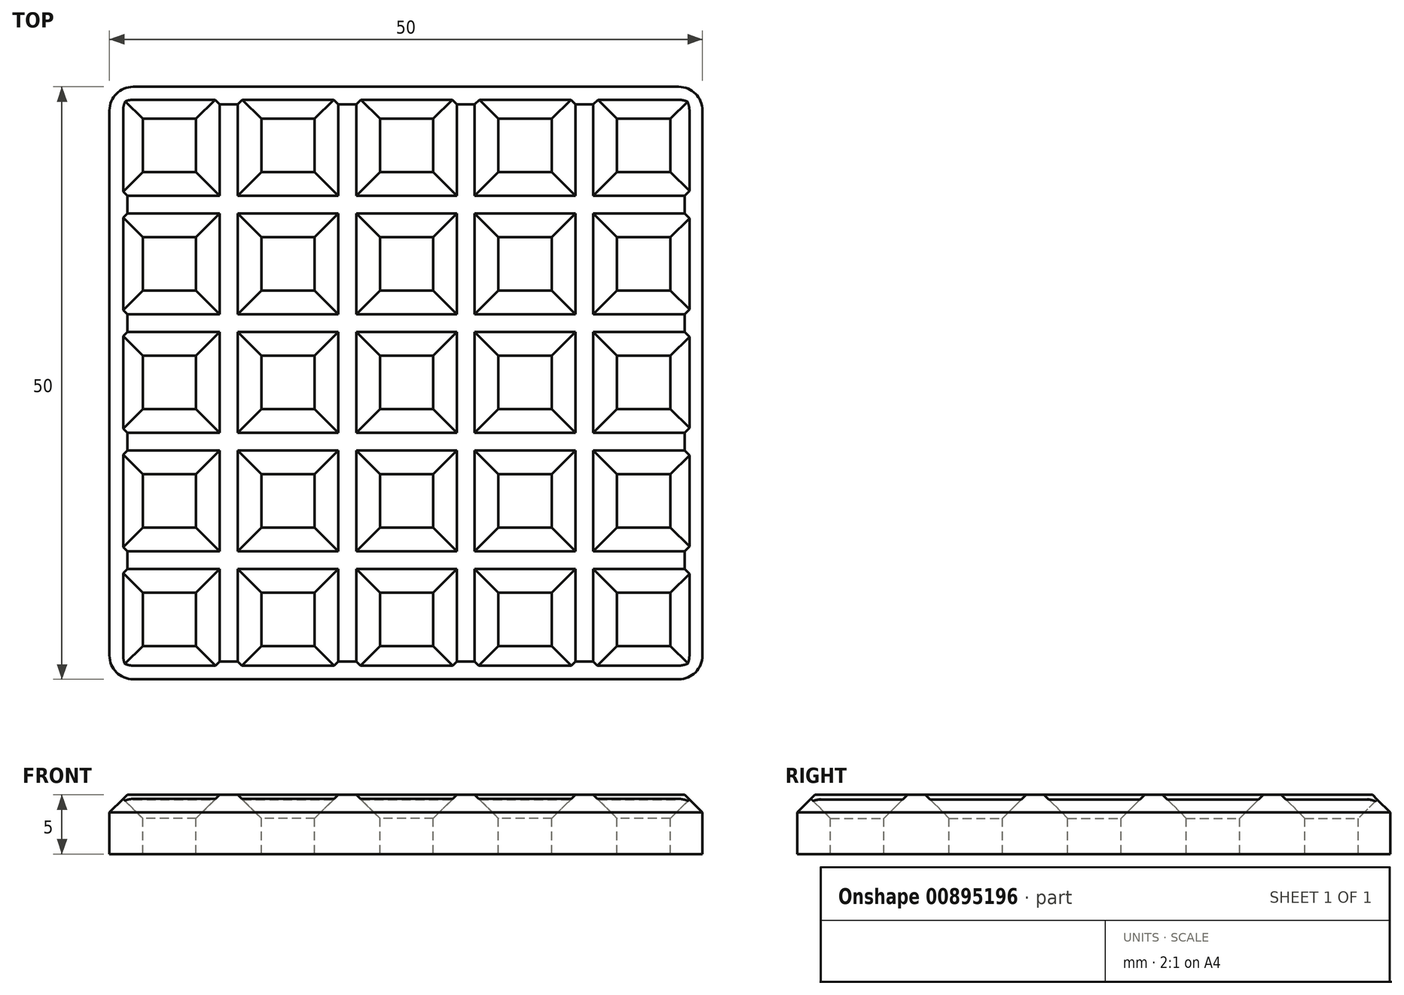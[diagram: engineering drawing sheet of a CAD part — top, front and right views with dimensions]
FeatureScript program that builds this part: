
annotation { "Feature Type Name" : "Feature", "Feature Type Description" : "" }
export const myFeature = defineFeature(function(context is Context, id is Id, definition is map)
    precondition{}
    {
        {
            var Q0;
            Q0=qCreatedBy(makeId("Top.planeOp"),FACE);
            var sketch = newSketch(context, id + "F0", { "sketchPlane" : qUnion([Q0])});
            skLineSegment(sketch, "E0.bottom", {"start": v(25, 25) * mm, "end": v(-25, 25) * mm});
            skLineSegment(sketch, "E0.top", {"start": v(25, -25) * mm, "end": v(-25, -25) * mm});
            skLineSegment(sketch, "E0.left", {"start": v(25, 25) * mm, "end": v(25, -25) * mm});
            skLineSegment(sketch, "E0.right", {"start": v(-25, 25) * mm, "end": v(-25, -25) * mm});
            skPoint(sketch, "E0.middle", {"position": v(0, 0) * mm});
            skLineSegment(sketch, "E1.bottom", {"start": v(-17.7, -17.7) * mm, "end": v(-22.2, -17.7) * mm});
            skLineSegment(sketch, "E1.top", {"start": v(-17.7, -22.2) * mm, "end": v(-22.2, -22.2) * mm});
            skLineSegment(sketch, "E1.left", {"start": v(-17.7, -17.7) * mm, "end": v(-17.7, -22.2) * mm});
            skLineSegment(sketch, "E1.right", {"start": v(-22.2, -17.7) * mm, "end": v(-22.2, -22.2) * mm});
            skPoint(sketch, "E1.middle", {"position": v(-19.95, -19.95) * mm});
            skLineSegment(sketch, "E2.0.1.0", {"start": v(-17.7, -7.7) * mm, "end": v(-17.7, -12.2) * mm});
            skLineSegment(sketch, "E2.0.1.1", {"start": v(-17.7, -7.7) * mm, "end": v(-22.2, -7.7) * mm});
            skLineSegment(sketch, "E2.0.1.2", {"start": v(-22.2, -7.7) * mm, "end": v(-22.2, -12.2) * mm});
            skLineSegment(sketch, "E2.0.1.3", {"start": v(-17.7, -12.2) * mm, "end": v(-22.2, -12.2) * mm});
            skLineSegment(sketch, "E2.0.2.0", {"start": v(-17.7, 2.3) * mm, "end": v(-17.7, -2.2) * mm});
            skLineSegment(sketch, "E2.0.2.1", {"start": v(-17.7, 2.3) * mm, "end": v(-22.2, 2.3) * mm});
            skLineSegment(sketch, "E2.0.2.2", {"start": v(-22.2, 2.3) * mm, "end": v(-22.2, -2.2) * mm});
            skLineSegment(sketch, "E2.0.2.3", {"start": v(-17.7, -2.2) * mm, "end": v(-22.2, -2.2) * mm});
            skLineSegment(sketch, "E2.0.3.0", {"start": v(-17.7, 12.3) * mm, "end": v(-17.7, 7.8) * mm});
            skLineSegment(sketch, "E2.0.3.1", {"start": v(-17.7, 12.3) * mm, "end": v(-22.2, 12.3) * mm});
            skLineSegment(sketch, "E2.0.3.2", {"start": v(-22.2, 12.3) * mm, "end": v(-22.2, 7.8) * mm});
            skLineSegment(sketch, "E2.0.3.3", {"start": v(-17.7, 7.8) * mm, "end": v(-22.2, 7.8) * mm});
            skLineSegment(sketch, "E2.0.4.0", {"start": v(-17.7, 22.3) * mm, "end": v(-17.7, 17.8) * mm});
            skLineSegment(sketch, "E2.0.4.1", {"start": v(-17.7, 22.3) * mm, "end": v(-22.2, 22.3) * mm});
            skLineSegment(sketch, "E2.0.4.2", {"start": v(-22.2, 22.3) * mm, "end": v(-22.2, 17.8) * mm});
            skLineSegment(sketch, "E2.0.4.3", {"start": v(-17.7, 17.8) * mm, "end": v(-22.2, 17.8) * mm});
            skLineSegment(sketch, "E2.1.0.0", {"start": v(-7.7, -17.7) * mm, "end": v(-7.7, -22.2) * mm});
            skLineSegment(sketch, "E2.1.0.1", {"start": v(-7.7, -17.7) * mm, "end": v(-12.2, -17.7) * mm});
            skLineSegment(sketch, "E2.1.0.2", {"start": v(-12.2, -17.7) * mm, "end": v(-12.2, -22.2) * mm});
            skLineSegment(sketch, "E2.1.0.3", {"start": v(-7.7, -22.2) * mm, "end": v(-12.2, -22.2) * mm});
            skLineSegment(sketch, "E2.1.1.0", {"start": v(-7.7, -7.7) * mm, "end": v(-7.7, -12.2) * mm});
            skLineSegment(sketch, "E2.1.1.1", {"start": v(-7.7, -7.7) * mm, "end": v(-12.2, -7.7) * mm});
            skLineSegment(sketch, "E2.1.1.2", {"start": v(-12.2, -7.7) * mm, "end": v(-12.2, -12.2) * mm});
            skLineSegment(sketch, "E2.1.1.3", {"start": v(-7.7, -12.2) * mm, "end": v(-12.2, -12.2) * mm});
            skLineSegment(sketch, "E2.1.2.0", {"start": v(-7.7, 2.3) * mm, "end": v(-7.7, -2.2) * mm});
            skLineSegment(sketch, "E2.1.2.1", {"start": v(-7.7, 2.3) * mm, "end": v(-12.2, 2.3) * mm});
            skLineSegment(sketch, "E2.1.2.2", {"start": v(-12.2, 2.3) * mm, "end": v(-12.2, -2.2) * mm});
            skLineSegment(sketch, "E2.1.2.3", {"start": v(-7.7, -2.2) * mm, "end": v(-12.2, -2.2) * mm});
            skLineSegment(sketch, "E2.1.3.0", {"start": v(-7.7, 12.3) * mm, "end": v(-7.7, 7.8) * mm});
            skLineSegment(sketch, "E2.1.3.1", {"start": v(-7.7, 12.3) * mm, "end": v(-12.2, 12.3) * mm});
            skLineSegment(sketch, "E2.1.3.2", {"start": v(-12.2, 12.3) * mm, "end": v(-12.2, 7.8) * mm});
            skLineSegment(sketch, "E2.1.3.3", {"start": v(-7.7, 7.8) * mm, "end": v(-12.2, 7.8) * mm});
            skLineSegment(sketch, "E2.1.4.0", {"start": v(-7.7, 22.3) * mm, "end": v(-7.7, 17.8) * mm});
            skLineSegment(sketch, "E2.1.4.1", {"start": v(-7.7, 22.3) * mm, "end": v(-12.2, 22.3) * mm});
            skLineSegment(sketch, "E2.1.4.2", {"start": v(-12.2, 22.3) * mm, "end": v(-12.2, 17.8) * mm});
            skLineSegment(sketch, "E2.1.4.3", {"start": v(-7.7, 17.8) * mm, "end": v(-12.2, 17.8) * mm});
            skLineSegment(sketch, "E2.2.0.0", {"start": v(2.3, -17.7) * mm, "end": v(2.3, -22.2) * mm});
            skLineSegment(sketch, "E2.2.0.1", {"start": v(2.3, -17.7) * mm, "end": v(-2.2, -17.7) * mm});
            skLineSegment(sketch, "E2.2.0.2", {"start": v(-2.2, -17.7) * mm, "end": v(-2.2, -22.2) * mm});
            skLineSegment(sketch, "E2.2.0.3", {"start": v(2.3, -22.2) * mm, "end": v(-2.2, -22.2) * mm});
            skLineSegment(sketch, "E2.2.1.0", {"start": v(2.3, -7.7) * mm, "end": v(2.3, -12.2) * mm});
            skLineSegment(sketch, "E2.2.1.1", {"start": v(2.3, -7.7) * mm, "end": v(-2.2, -7.7) * mm});
            skLineSegment(sketch, "E2.2.1.2", {"start": v(-2.2, -7.7) * mm, "end": v(-2.2, -12.2) * mm});
            skLineSegment(sketch, "E2.2.1.3", {"start": v(2.3, -12.2) * mm, "end": v(-2.2, -12.2) * mm});
            skLineSegment(sketch, "E2.2.2.0", {"start": v(2.3, 2.3) * mm, "end": v(2.3, -2.2) * mm});
            skLineSegment(sketch, "E2.2.2.1", {"start": v(2.3, 2.3) * mm, "end": v(-2.2, 2.3) * mm});
            skLineSegment(sketch, "E2.2.2.2", {"start": v(-2.2, 2.3) * mm, "end": v(-2.2, -2.2) * mm});
            skLineSegment(sketch, "E2.2.2.3", {"start": v(2.3, -2.2) * mm, "end": v(-2.2, -2.2) * mm});
            skLineSegment(sketch, "E2.2.3.0", {"start": v(2.3, 12.3) * mm, "end": v(2.3, 7.8) * mm});
            skLineSegment(sketch, "E2.2.3.1", {"start": v(2.3, 12.3) * mm, "end": v(-2.2, 12.3) * mm});
            skLineSegment(sketch, "E2.2.3.2", {"start": v(-2.2, 12.3) * mm, "end": v(-2.2, 7.8) * mm});
            skLineSegment(sketch, "E2.2.3.3", {"start": v(2.3, 7.8) * mm, "end": v(-2.2, 7.8) * mm});
            skLineSegment(sketch, "E2.2.4.0", {"start": v(2.3, 22.3) * mm, "end": v(2.3, 17.8) * mm});
            skLineSegment(sketch, "E2.2.4.1", {"start": v(2.3, 22.3) * mm, "end": v(-2.2, 22.3) * mm});
            skLineSegment(sketch, "E2.2.4.2", {"start": v(-2.2, 22.3) * mm, "end": v(-2.2, 17.8) * mm});
            skLineSegment(sketch, "E2.2.4.3", {"start": v(2.3, 17.8) * mm, "end": v(-2.2, 17.8) * mm});
            skLineSegment(sketch, "E2.3.0.0", {"start": v(12.3, -17.7) * mm, "end": v(12.3, -22.2) * mm});
            skLineSegment(sketch, "E2.3.0.1", {"start": v(12.3, -17.7) * mm, "end": v(7.8, -17.7) * mm});
            skLineSegment(sketch, "E2.3.0.2", {"start": v(7.8, -17.7) * mm, "end": v(7.8, -22.2) * mm});
            skLineSegment(sketch, "E2.3.0.3", {"start": v(12.3, -22.2) * mm, "end": v(7.8, -22.2) * mm});
            skLineSegment(sketch, "E2.3.1.0", {"start": v(12.3, -7.7) * mm, "end": v(12.3, -12.2) * mm});
            skLineSegment(sketch, "E2.3.1.1", {"start": v(12.3, -7.7) * mm, "end": v(7.8, -7.7) * mm});
            skLineSegment(sketch, "E2.3.1.2", {"start": v(7.8, -7.7) * mm, "end": v(7.8, -12.2) * mm});
            skLineSegment(sketch, "E2.3.1.3", {"start": v(12.3, -12.2) * mm, "end": v(7.8, -12.2) * mm});
            skLineSegment(sketch, "E2.3.2.0", {"start": v(12.3, 2.3) * mm, "end": v(12.3, -2.2) * mm});
            skLineSegment(sketch, "E2.3.2.1", {"start": v(12.3, 2.3) * mm, "end": v(7.8, 2.3) * mm});
            skLineSegment(sketch, "E2.3.2.2", {"start": v(7.8, 2.3) * mm, "end": v(7.8, -2.2) * mm});
            skLineSegment(sketch, "E2.3.2.3", {"start": v(12.3, -2.2) * mm, "end": v(7.8, -2.2) * mm});
            skLineSegment(sketch, "E2.3.3.0", {"start": v(12.3, 12.3) * mm, "end": v(12.3, 7.8) * mm});
            skLineSegment(sketch, "E2.3.3.1", {"start": v(12.3, 12.3) * mm, "end": v(7.8, 12.3) * mm});
            skLineSegment(sketch, "E2.3.3.2", {"start": v(7.8, 12.3) * mm, "end": v(7.8, 7.8) * mm});
            skLineSegment(sketch, "E2.3.3.3", {"start": v(12.3, 7.8) * mm, "end": v(7.8, 7.8) * mm});
            skLineSegment(sketch, "E2.3.4.0", {"start": v(12.3, 22.3) * mm, "end": v(12.3, 17.8) * mm});
            skLineSegment(sketch, "E2.3.4.1", {"start": v(12.3, 22.3) * mm, "end": v(7.8, 22.3) * mm});
            skLineSegment(sketch, "E2.3.4.2", {"start": v(7.8, 22.3) * mm, "end": v(7.8, 17.8) * mm});
            skLineSegment(sketch, "E2.3.4.3", {"start": v(12.3, 17.8) * mm, "end": v(7.8, 17.8) * mm});
            skLineSegment(sketch, "E2.4.0.0", {"start": v(22.3, -17.7) * mm, "end": v(22.3, -22.2) * mm});
            skLineSegment(sketch, "E2.4.0.1", {"start": v(22.3, -17.7) * mm, "end": v(17.8, -17.7) * mm});
            skLineSegment(sketch, "E2.4.0.2", {"start": v(17.8, -17.7) * mm, "end": v(17.8, -22.2) * mm});
            skLineSegment(sketch, "E2.4.0.3", {"start": v(22.3, -22.2) * mm, "end": v(17.8, -22.2) * mm});
            skLineSegment(sketch, "E2.4.1.0", {"start": v(22.3, -7.7) * mm, "end": v(22.3, -12.2) * mm});
            skLineSegment(sketch, "E2.4.1.1", {"start": v(22.3, -7.7) * mm, "end": v(17.8, -7.7) * mm});
            skLineSegment(sketch, "E2.4.1.2", {"start": v(17.8, -7.7) * mm, "end": v(17.8, -12.2) * mm});
            skLineSegment(sketch, "E2.4.1.3", {"start": v(22.3, -12.2) * mm, "end": v(17.8, -12.2) * mm});
            skLineSegment(sketch, "E2.4.2.0", {"start": v(22.3, 2.3) * mm, "end": v(22.3, -2.2) * mm});
            skLineSegment(sketch, "E2.4.2.1", {"start": v(22.3, 2.3) * mm, "end": v(17.8, 2.3) * mm});
            skLineSegment(sketch, "E2.4.2.2", {"start": v(17.8, 2.3) * mm, "end": v(17.8, -2.2) * mm});
            skLineSegment(sketch, "E2.4.2.3", {"start": v(22.3, -2.2) * mm, "end": v(17.8, -2.2) * mm});
            skLineSegment(sketch, "E2.4.3.0", {"start": v(22.3, 12.3) * mm, "end": v(22.3, 7.8) * mm});
            skLineSegment(sketch, "E2.4.3.1", {"start": v(22.3, 12.3) * mm, "end": v(17.8, 12.3) * mm});
            skLineSegment(sketch, "E2.4.3.2", {"start": v(17.8, 12.3) * mm, "end": v(17.8, 7.8) * mm});
            skLineSegment(sketch, "E2.4.3.3", {"start": v(22.3, 7.8) * mm, "end": v(17.8, 7.8) * mm});
            skLineSegment(sketch, "E2.4.4.0", {"start": v(22.3, 22.3) * mm, "end": v(22.3, 17.8) * mm});
            skLineSegment(sketch, "E2.4.4.1", {"start": v(22.3, 22.3) * mm, "end": v(17.8, 22.3) * mm});
            skLineSegment(sketch, "E2.4.4.2", {"start": v(17.8, 22.3) * mm, "end": v(17.8, 17.8) * mm});
            skLineSegment(sketch, "E2.4.4.3", {"start": v(22.3, 17.8) * mm, "end": v(17.8, 17.8) * mm});
            skLineSegment(sketch, "E2.direction1", {"start": v(-17.7, -22.2) * mm, "end": v(-7.7, -22.2) * mm, "construction": true});
            skLineSegment(sketch, "E2.direction2", {"start": v(-17.7, -22.2) * mm, "end": v(-17.7, -12.2) * mm, "construction": true});
            skSolve(sketch);
        }
        {
            var Q0;
            Q0=makeQuery(id+"F0.imprint","IMPRINT",FACE,{"disambiguationData":[TD([[makeQuery(id+"F0.imprint","IMPRINT",EDGE,{"derivedFrom":sQuery(id+"F0.wireOp",EDGE,"E0.bottom")}),1.0]])]});
            extrude(context, id + "F1", {"entities" : qUnion([Q0]), "oppositeDirection" : true, "depth" : 5 * mm, "offsetDistance" : 25 * mm});
        }
        {
            var Q0;
            Q0=makeQuery(id+"F1.opExtrude","CAP_EDGE",EDGE,{"disambiguationData":[OSD([sQuery(id+"F0.wireOp",EDGE,"E2.0.1.2")])],"isStart":true});
            var Q1;
            Q1=makeQuery(id+"F1.opExtrude","CAP_EDGE",EDGE,{"disambiguationData":[OSD([sQuery(id+"F0.wireOp",EDGE,"E1.right")])],"isStart":true});
            var Q2;
            Q2=makeQuery(id+"F1.opExtrude","CAP_EDGE",EDGE,{"disambiguationData":[OSD([sQuery(id+"F0.wireOp",EDGE,"E1.top")])],"isStart":true});
            var Q3;
            Q3=makeQuery(id+"F1.opExtrude","CAP_EDGE",EDGE,{"disambiguationData":[OSD([sQuery(id+"F0.wireOp",EDGE,"E1.left")])],"isStart":true});
            var Q4;
            Q4=makeQuery(id+"F1.opExtrude","CAP_EDGE",EDGE,{"disambiguationData":[OSD([sQuery(id+"F0.wireOp",EDGE,"E1.bottom")])],"isStart":true});
            var Q5;
            Q5=makeQuery(id+"F1.opExtrude","CAP_EDGE",EDGE,{"disambiguationData":[OSD([sQuery(id+"F0.wireOp",EDGE,"E2.0.1.0")])],"isStart":true});
            var Q6;
            Q6=makeQuery(id+"F1.opExtrude","CAP_EDGE",EDGE,{"disambiguationData":[OSD([sQuery(id+"F0.wireOp",EDGE,"E2.0.1.1")])],"isStart":true});
            var Q7;
            Q7=makeQuery(id+"F1.opExtrude","CAP_EDGE",EDGE,{"disambiguationData":[OSD([sQuery(id+"F0.wireOp",EDGE,"E2.0.2.1")])],"isStart":true});
            var Q8;
            Q8=makeQuery(id+"F1.opExtrude","CAP_EDGE",EDGE,{"disambiguationData":[OSD([sQuery(id+"F0.wireOp",EDGE,"E2.0.2.2")])],"isStart":true});
            var Q9;
            Q9=makeQuery(id+"F1.opExtrude","CAP_EDGE",EDGE,{"disambiguationData":[OSD([sQuery(id+"F0.wireOp",EDGE,"E2.1.2.3")])],"isStart":true});
            var Q10;
            Q10=makeQuery(id+"F1.opExtrude","CAP_EDGE",EDGE,{"disambiguationData":[OSD([sQuery(id+"F0.wireOp",EDGE,"E2.1.2.1")])],"isStart":true});
            var Q11;
            Q11=makeQuery(id+"F1.opExtrude","CAP_EDGE",EDGE,{"disambiguationData":[OSD([sQuery(id+"F0.wireOp",EDGE,"E2.1.2.2")])],"isStart":true});
            var Q12;
            Q12=makeQuery(id+"F1.opExtrude","CAP_EDGE",EDGE,{"disambiguationData":[OSD([sQuery(id+"F0.wireOp",EDGE,"E2.1.2.0")])],"isStart":true});
            var Q13;
            Q13=makeQuery(id+"F1.opExtrude","CAP_EDGE",EDGE,{"disambiguationData":[OSD([sQuery(id+"F0.wireOp",EDGE,"E2.1.1.1")])],"isStart":true});
            var Q14;
            Q14=makeQuery(id+"F1.opExtrude","CAP_EDGE",EDGE,{"disambiguationData":[OSD([sQuery(id+"F0.wireOp",EDGE,"E2.1.1.3")])],"isStart":true});
            var Q15;
            Q15=makeQuery(id+"F1.opExtrude","CAP_EDGE",EDGE,{"disambiguationData":[OSD([sQuery(id+"F0.wireOp",EDGE,"E2.1.1.2")])],"isStart":true});
            var Q16;
            Q16=makeQuery(id+"F1.opExtrude","CAP_EDGE",EDGE,{"disambiguationData":[OSD([sQuery(id+"F0.wireOp",EDGE,"E2.1.1.0")])],"isStart":true});
            var Q17;
            Q17=makeQuery(id+"F1.opExtrude","CAP_EDGE",EDGE,{"disambiguationData":[OSD([sQuery(id+"F0.wireOp",EDGE,"E2.1.0.1")])],"isStart":true});
            var Q18;
            Q18=makeQuery(id+"F1.opExtrude","CAP_EDGE",EDGE,{"disambiguationData":[OSD([sQuery(id+"F0.wireOp",EDGE,"E2.1.0.2")])],"isStart":true});
            var Q19;
            Q19=makeQuery(id+"F1.opExtrude","CAP_EDGE",EDGE,{"disambiguationData":[OSD([sQuery(id+"F0.wireOp",EDGE,"E2.1.0.3")])],"isStart":true});
            var Q20;
            Q20=makeQuery(id+"F1.opExtrude","CAP_EDGE",EDGE,{"disambiguationData":[OSD([sQuery(id+"F0.wireOp",EDGE,"E2.1.0.0")])],"isStart":true});
            var Q21;
            Q21=makeQuery(id+"F1.opExtrude","CAP_EDGE",EDGE,{"disambiguationData":[OSD([sQuery(id+"F0.wireOp",EDGE,"E2.2.0.2")])],"isStart":true});
            var Q22;
            Q22=makeQuery(id+"F1.opExtrude","CAP_EDGE",EDGE,{"disambiguationData":[OSD([sQuery(id+"F0.wireOp",EDGE,"E2.2.0.1")])],"isStart":true});
            var Q23;
            Q23=makeQuery(id+"F1.opExtrude","CAP_EDGE",EDGE,{"disambiguationData":[OSD([sQuery(id+"F0.wireOp",EDGE,"E2.2.0.3")])],"isStart":true});
            var Q24;
            Q24=makeQuery(id+"F1.opExtrude","CAP_EDGE",EDGE,{"disambiguationData":[OSD([sQuery(id+"F0.wireOp",EDGE,"E2.2.1.0")])],"isStart":true});
            var Q25;
            Q25=makeQuery(id+"F1.opExtrude","CAP_EDGE",EDGE,{"disambiguationData":[OSD([sQuery(id+"F0.wireOp",EDGE,"E2.2.1.1")])],"isStart":true});
            var Q26;
            Q26=makeQuery(id+"F1.opExtrude","CAP_EDGE",EDGE,{"disambiguationData":[OSD([sQuery(id+"F0.wireOp",EDGE,"E2.2.1.2")])],"isStart":true});
            var Q27;
            Q27=makeQuery(id+"F1.opExtrude","CAP_EDGE",EDGE,{"disambiguationData":[OSD([sQuery(id+"F0.wireOp",EDGE,"E2.2.1.3")])],"isStart":true});
            var Q28;
            Q28=makeQuery(id+"F1.opExtrude","CAP_EDGE",EDGE,{"disambiguationData":[OSD([sQuery(id+"F0.wireOp",EDGE,"E2.2.2.1")])],"isStart":true});
            var Q29;
            Q29=makeQuery(id+"F1.opExtrude","CAP_EDGE",EDGE,{"disambiguationData":[OSD([sQuery(id+"F0.wireOp",EDGE,"E2.2.2.2")])],"isStart":true});
            var Q30;
            Q30=makeQuery(id+"F1.opExtrude","CAP_EDGE",EDGE,{"disambiguationData":[OSD([sQuery(id+"F0.wireOp",EDGE,"E2.2.2.3")])],"isStart":true});
            var Q31;
            Q31=makeQuery(id+"F1.opExtrude","CAP_EDGE",EDGE,{"disambiguationData":[OSD([sQuery(id+"F0.wireOp",EDGE,"E2.2.2.0")])],"isStart":true});
            var Q32;
            Q32=makeQuery(id+"F1.opExtrude","CAP_EDGE",EDGE,{"disambiguationData":[OSD([sQuery(id+"F0.wireOp",EDGE,"E2.2.3.3")])],"isStart":true});
            var Q33;
            Q33=makeQuery(id+"F1.opExtrude","CAP_EDGE",EDGE,{"disambiguationData":[OSD([sQuery(id+"F0.wireOp",EDGE,"E2.2.3.1")])],"isStart":true});
            var Q34;
            Q34=makeQuery(id+"F1.opExtrude","CAP_EDGE",EDGE,{"disambiguationData":[OSD([sQuery(id+"F0.wireOp",EDGE,"E2.2.3.2")])],"isStart":true});
            var Q35;
            Q35=makeQuery(id+"F1.opExtrude","CAP_EDGE",EDGE,{"disambiguationData":[OSD([sQuery(id+"F0.wireOp",EDGE,"E2.1.3.0")])],"isStart":true});
            var Q36;
            Q36=makeQuery(id+"F1.opExtrude","CAP_EDGE",EDGE,{"disambiguationData":[OSD([sQuery(id+"F0.wireOp",EDGE,"E2.1.3.1")])],"isStart":true});
            var Q37;
            Q37=makeQuery(id+"F1.opExtrude","CAP_EDGE",EDGE,{"disambiguationData":[OSD([sQuery(id+"F0.wireOp",EDGE,"E2.1.3.2")])],"isStart":true});
            var Q38;
            Q38=makeQuery(id+"F1.opExtrude","CAP_EDGE",EDGE,{"disambiguationData":[OSD([sQuery(id+"F0.wireOp",EDGE,"E2.1.3.3")])],"isStart":true});
            var Q39;
            Q39=makeQuery(id+"F1.opExtrude","CAP_EDGE",EDGE,{"disambiguationData":[OSD([sQuery(id+"F0.wireOp",EDGE,"E2.0.3.0")])],"isStart":true});
            var Q40;
            Q40=makeQuery(id+"F1.opExtrude","CAP_EDGE",EDGE,{"disambiguationData":[OSD([sQuery(id+"F0.wireOp",EDGE,"E2.0.3.1")])],"isStart":true});
            var Q41;
            Q41=makeQuery(id+"F1.opExtrude","CAP_EDGE",EDGE,{"disambiguationData":[OSD([sQuery(id+"F0.wireOp",EDGE,"E2.0.3.2")])],"isStart":true});
            var Q42;
            Q42=makeQuery(id+"F1.opExtrude","CAP_EDGE",EDGE,{"disambiguationData":[OSD([sQuery(id+"F0.wireOp",EDGE,"E2.0.3.3")])],"isStart":true});
            var Q43;
            Q43=makeQuery(id+"F1.opExtrude","CAP_EDGE",EDGE,{"disambiguationData":[OSD([sQuery(id+"F0.wireOp",EDGE,"E2.0.4.2")])],"isStart":true});
            var Q44;
            Q44=makeQuery(id+"F1.opExtrude","CAP_EDGE",EDGE,{"disambiguationData":[OSD([sQuery(id+"F0.wireOp",EDGE,"E2.0.4.1")])],"isStart":true});
            var Q45;
            Q45=makeQuery(id+"F1.opExtrude","CAP_EDGE",EDGE,{"disambiguationData":[OSD([sQuery(id+"F0.wireOp",EDGE,"E2.0.4.3")])],"isStart":true});
            var Q46;
            Q46=makeQuery(id+"F1.opExtrude","CAP_EDGE",EDGE,{"disambiguationData":[OSD([sQuery(id+"F0.wireOp",EDGE,"E2.0.4.0")])],"isStart":true});
            var Q47;
            Q47=makeQuery(id+"F1.opExtrude","CAP_EDGE",EDGE,{"disambiguationData":[OSD([sQuery(id+"F0.wireOp",EDGE,"E2.1.4.1")])],"isStart":true});
            var Q48;
            Q48=makeQuery(id+"F1.opExtrude","CAP_EDGE",EDGE,{"disambiguationData":[OSD([sQuery(id+"F0.wireOp",EDGE,"E2.1.4.2")])],"isStart":true});
            var Q49;
            Q49=makeQuery(id+"F1.opExtrude","CAP_EDGE",EDGE,{"disambiguationData":[OSD([sQuery(id+"F0.wireOp",EDGE,"E2.1.4.3")])],"isStart":true});
            var Q50;
            Q50=makeQuery(id+"F1.opExtrude","CAP_EDGE",EDGE,{"disambiguationData":[OSD([sQuery(id+"F0.wireOp",EDGE,"E2.1.4.0")])],"isStart":true});
            var Q51;
            Q51=makeQuery(id+"F1.opExtrude","CAP_EDGE",EDGE,{"disambiguationData":[OSD([sQuery(id+"F0.wireOp",EDGE,"E2.2.4.1")])],"isStart":true});
            var Q52;
            Q52=makeQuery(id+"F1.opExtrude","CAP_EDGE",EDGE,{"disambiguationData":[OSD([sQuery(id+"F0.wireOp",EDGE,"E2.2.4.3")])],"isStart":true});
            var Q53;
            Q53=makeQuery(id+"F1.opExtrude","CAP_EDGE",EDGE,{"disambiguationData":[OSD([sQuery(id+"F0.wireOp",EDGE,"E2.2.4.2")])],"isStart":true});
            var Q54;
            Q54=makeQuery(id+"F1.opExtrude","CAP_EDGE",EDGE,{"disambiguationData":[OSD([sQuery(id+"F0.wireOp",EDGE,"E2.2.4.0")])],"isStart":true});
            var Q55;
            Q55=makeQuery(id+"F1.opExtrude","CAP_EDGE",EDGE,{"disambiguationData":[OSD([sQuery(id+"F0.wireOp",EDGE,"E2.3.3.1")])],"isStart":true});
            var Q56;
            Q56=makeQuery(id+"F1.opExtrude","CAP_EDGE",EDGE,{"disambiguationData":[OSD([sQuery(id+"F0.wireOp",EDGE,"E2.3.3.2")])],"isStart":true});
            var Q57;
            Q57=makeQuery(id+"F1.opExtrude","CAP_EDGE",EDGE,{"disambiguationData":[OSD([sQuery(id+"F0.wireOp",EDGE,"E2.3.3.3")])],"isStart":true});
            var Q58;
            Q58=makeQuery(id+"F1.opExtrude","CAP_EDGE",EDGE,{"disambiguationData":[OSD([sQuery(id+"F0.wireOp",EDGE,"E2.3.3.0")])],"isStart":true});
            var Q59;
            Q59=makeQuery(id+"F1.opExtrude","CAP_EDGE",EDGE,{"disambiguationData":[OSD([sQuery(id+"F0.wireOp",EDGE,"E2.3.4.1")])],"isStart":true});
            var Q60;
            Q60=makeQuery(id+"F1.opExtrude","CAP_EDGE",EDGE,{"disambiguationData":[OSD([sQuery(id+"F0.wireOp",EDGE,"E2.3.4.2")])],"isStart":true});
            var Q61;
            Q61=makeQuery(id+"F1.opExtrude","CAP_EDGE",EDGE,{"disambiguationData":[OSD([sQuery(id+"F0.wireOp",EDGE,"E2.3.4.3")])],"isStart":true});
            var Q62;
            Q62=makeQuery(id+"F1.opExtrude","CAP_EDGE",EDGE,{"disambiguationData":[OSD([sQuery(id+"F0.wireOp",EDGE,"E2.3.4.0")])],"isStart":true});
            var Q63;
            Q63=makeQuery(id+"F1.opExtrude","CAP_EDGE",EDGE,{"disambiguationData":[OSD([sQuery(id+"F0.wireOp",EDGE,"E2.4.4.2")])],"isStart":true});
            var Q64;
            Q64=makeQuery(id+"F1.opExtrude","CAP_EDGE",EDGE,{"disambiguationData":[OSD([sQuery(id+"F0.wireOp",EDGE,"E2.4.4.1")])],"isStart":true});
            var Q65;
            Q65=makeQuery(id+"F1.opExtrude","CAP_EDGE",EDGE,{"disambiguationData":[OSD([sQuery(id+"F0.wireOp",EDGE,"E2.4.4.0")])],"isStart":true});
            var Q66;
            Q66=makeQuery(id+"F1.opExtrude","CAP_EDGE",EDGE,{"disambiguationData":[OSD([sQuery(id+"F0.wireOp",EDGE,"E2.4.4.3")])],"isStart":true});
            var Q67;
            Q67=makeQuery(id+"F1.opExtrude","CAP_EDGE",EDGE,{"disambiguationData":[OSD([sQuery(id+"F0.wireOp",EDGE,"E2.4.3.1")])],"isStart":true});
            var Q68;
            Q68=makeQuery(id+"F1.opExtrude","CAP_EDGE",EDGE,{"disambiguationData":[OSD([sQuery(id+"F0.wireOp",EDGE,"E2.4.3.2")])],"isStart":true});
            var Q69;
            Q69=makeQuery(id+"F1.opExtrude","CAP_EDGE",EDGE,{"disambiguationData":[OSD([sQuery(id+"F0.wireOp",EDGE,"E2.4.3.0")])],"isStart":true});
            var Q70;
            Q70=makeQuery(id+"F1.opExtrude","CAP_EDGE",EDGE,{"disambiguationData":[OSD([sQuery(id+"F0.wireOp",EDGE,"E2.4.3.3")])],"isStart":true});
            var Q71;
            Q71=makeQuery(id+"F1.opExtrude","CAP_EDGE",EDGE,{"disambiguationData":[OSD([sQuery(id+"F0.wireOp",EDGE,"E2.4.2.1")])],"isStart":true});
            var Q72;
            Q72=makeQuery(id+"F1.opExtrude","CAP_EDGE",EDGE,{"disambiguationData":[OSD([sQuery(id+"F0.wireOp",EDGE,"E2.3.2.2")])],"isStart":true});
            var Q73;
            Q73=makeQuery(id+"F1.opExtrude","CAP_EDGE",EDGE,{"disambiguationData":[OSD([sQuery(id+"F0.wireOp",EDGE,"E2.3.2.3")])],"isStart":true});
            var Q74;
            Q74=makeQuery(id+"F1.opExtrude","CAP_EDGE",EDGE,{"disambiguationData":[OSD([sQuery(id+"F0.wireOp",EDGE,"E2.3.2.0")])],"isStart":true});
            var Q75;
            Q75=makeQuery(id+"F1.opExtrude","CAP_EDGE",EDGE,{"disambiguationData":[OSD([sQuery(id+"F0.wireOp",EDGE,"E2.3.2.1")])],"isStart":true});
            var Q76;
            Q76=makeQuery(id+"F1.opExtrude","CAP_EDGE",EDGE,{"disambiguationData":[OSD([sQuery(id+"F0.wireOp",EDGE,"E2.4.2.2")])],"isStart":true});
            var Q77;
            Q77=makeQuery(id+"F1.opExtrude","CAP_EDGE",EDGE,{"disambiguationData":[OSD([sQuery(id+"F0.wireOp",EDGE,"E2.4.2.3")])],"isStart":true});
            var Q78;
            Q78=makeQuery(id+"F1.opExtrude","CAP_EDGE",EDGE,{"disambiguationData":[OSD([sQuery(id+"F0.wireOp",EDGE,"E2.4.2.0")])],"isStart":true});
            var Q79;
            Q79=makeQuery(id+"F1.opExtrude","CAP_EDGE",EDGE,{"disambiguationData":[OSD([sQuery(id+"F0.wireOp",EDGE,"E2.4.1.1")])],"isStart":true});
            var Q80;
            Q80=makeQuery(id+"F1.opExtrude","CAP_EDGE",EDGE,{"disambiguationData":[OSD([sQuery(id+"F0.wireOp",EDGE,"E2.3.1.1")])],"isStart":true});
            var Q81;
            Q81=makeQuery(id+"F1.opExtrude","CAP_EDGE",EDGE,{"disambiguationData":[OSD([sQuery(id+"F0.wireOp",EDGE,"E2.3.1.2")])],"isStart":true});
            var Q82;
            Q82=makeQuery(id+"F1.opExtrude","CAP_EDGE",EDGE,{"disambiguationData":[OSD([sQuery(id+"F0.wireOp",EDGE,"E2.3.0.1")])],"isStart":true});
            var Q83;
            Q83=makeQuery(id+"F1.opExtrude","CAP_EDGE",EDGE,{"disambiguationData":[OSD([sQuery(id+"F0.wireOp",EDGE,"E2.3.0.2")])],"isStart":true});
            var Q84;
            Q84=makeQuery(id+"F1.opExtrude","CAP_EDGE",EDGE,{"disambiguationData":[OSD([sQuery(id+"F0.wireOp",EDGE,"E2.4.1.2")])],"isStart":true});
            var Q85;
            Q85=makeQuery(id+"F1.opExtrude","CAP_EDGE",EDGE,{"disambiguationData":[OSD([sQuery(id+"F0.wireOp",EDGE,"E2.3.1.3")])],"isStart":true});
            var Q86;
            Q86=makeQuery(id+"F1.opExtrude","CAP_EDGE",EDGE,{"disambiguationData":[OSD([sQuery(id+"F0.wireOp",EDGE,"E2.4.0.1")])],"isStart":true});
            var Q87;
            Q87=makeQuery(id+"F1.opExtrude","CAP_EDGE",EDGE,{"disambiguationData":[OSD([sQuery(id+"F0.wireOp",EDGE,"E2.4.0.2")])],"isStart":true});
            var Q88;
            Q88=makeQuery(id+"F1.opExtrude","CAP_EDGE",EDGE,{"disambiguationData":[OSD([sQuery(id+"F0.wireOp",EDGE,"E2.4.0.3")])],"isStart":true});
            var Q89;
            Q89=makeQuery(id+"F1.opExtrude","CAP_EDGE",EDGE,{"disambiguationData":[OSD([sQuery(id+"F0.wireOp",EDGE,"E2.4.0.0")])],"isStart":true});
            var Q90;
            Q90=makeQuery(id+"F1.opExtrude","CAP_EDGE",EDGE,{"disambiguationData":[OSD([sQuery(id+"F0.wireOp",EDGE,"E2.3.0.3")])],"isStart":true});
            var Q91;
            Q91=makeQuery(id+"F1.opExtrude","CAP_EDGE",EDGE,{"disambiguationData":[OSD([sQuery(id+"F0.wireOp",EDGE,"E2.4.1.0")])],"isStart":true});
            var Q92;
            Q92=makeQuery(id+"F1.opExtrude","CAP_EDGE",EDGE,{"disambiguationData":[OSD([sQuery(id+"F0.wireOp",EDGE,"E2.4.1.3")])],"isStart":true});
            var Q93;
            Q93=makeQuery(id+"F1.opExtrude","CAP_EDGE",EDGE,{"disambiguationData":[OSD([sQuery(id+"F0.wireOp",EDGE,"E2.0.1.3")])],"isStart":true});
            var Q94;
            Q94=makeQuery(id+"F1.opExtrude","CAP_EDGE",EDGE,{"disambiguationData":[OSD([sQuery(id+"F0.wireOp",EDGE,"E2.0.2.3")])],"isStart":true});
            var Q95;
            Q95=makeQuery(id+"F1.opExtrude","CAP_EDGE",EDGE,{"disambiguationData":[OSD([sQuery(id+"F0.wireOp",EDGE,"E2.0.2.0")])],"isStart":true});
            var Q96;
            Q96=makeQuery(id+"F1.opExtrude","CAP_EDGE",EDGE,{"disambiguationData":[OSD([sQuery(id+"F0.wireOp",EDGE,"E2.2.0.0")])],"isStart":true});
            var Q97;
            Q97=makeQuery(id+"F1.opExtrude","CAP_EDGE",EDGE,{"disambiguationData":[OSD([sQuery(id+"F0.wireOp",EDGE,"E2.3.1.0")])],"isStart":true});
            var Q98;
            Q98=makeQuery(id+"F1.opExtrude","CAP_EDGE",EDGE,{"disambiguationData":[OSD([sQuery(id+"F0.wireOp",EDGE,"E2.3.0.0")])],"isStart":true});
            var Q99;
            Q99=makeQuery(id+"F1.opExtrude","CAP_EDGE",EDGE,{"disambiguationData":[OSD([sQuery(id+"F0.wireOp",EDGE,"E2.2.3.0")])],"isStart":true});
            chamfer(context, id + "F2", {"entities" : qUnion([Q0, Q1, Q2, Q3, Q4, Q5, Q6, Q7, Q8, Q9, Q10, Q11, Q12, Q13, Q14, Q15, Q16, Q17, Q18, Q19, Q20, Q21, Q22, Q23, Q24, Q25, Q26, Q27, Q28, Q29, Q30, Q31, Q32, Q33, Q34, Q35, Q36, Q37, Q38, Q39, Q40, Q41, Q42, Q43, Q44, Q45, Q46, Q47, Q48, Q49, Q50, Q51, Q52, Q53, Q54, Q55, Q56, Q57, Q58, Q59, Q60, Q61, Q62, Q63, Q64, Q65, Q66, Q67, Q68, Q69, Q70, Q71, Q72, Q73, Q74, Q75, Q76, Q77, Q78, Q79, Q80, Q81, Q82, Q83, Q84, Q85, Q86, Q87, Q88, Q89, Q90, Q91, Q92, Q93, Q94, Q95, Q96, Q97, Q98, Q99]), "width" : 2 * mm, "tangentPropagation" : true});
        }
        {
            var Q0;
            Q0=makeQuery(id+"F1.opExtrude","SWEPT_EDGE",EDGE,{"disambiguationData":[OSD([sQuery(id+"F0.wireOp",EDGE,"E0.bottom"),sQuery(id+"F0.wireOp",EDGE,"E0.left")])]});
            var Q1;
            Q1=makeQuery(id+"F1.opExtrude","SWEPT_EDGE",EDGE,{"disambiguationData":[OSD([sQuery(id+"F0.wireOp",EDGE,"E0.top"),sQuery(id+"F0.wireOp",EDGE,"E0.left")])]});
            var Q2;
            Q2=makeQuery(id+"F1.opExtrude","SWEPT_EDGE",EDGE,{"disambiguationData":[OSD([sQuery(id+"F0.wireOp",EDGE,"E0.top"),sQuery(id+"F0.wireOp",EDGE,"E0.right")])]});
            var Q3;
            Q3=makeQuery(id+"F1.opExtrude","SWEPT_EDGE",EDGE,{"disambiguationData":[OSD([sQuery(id+"F0.wireOp",EDGE,"E0.bottom"),sQuery(id+"F0.wireOp",EDGE,"E0.right")])]});
            fillet(context, id + "F3", {"entities" : qUnion([Q0, Q1, Q2, Q3]), "radius" : 2 * mm, "tangentPropagation" : true, "allowEdgeOverflow" : false});
        }
        {
            var Q0;
            Q0=makeQuery(id+"F1.opExtrude","CAP_EDGE",EDGE,{"disambiguationData":[OSD([sQuery(id+"F0.wireOp",EDGE,"E0.bottom")])],"isStart":true});
            var Q1;
            Q1=makeQuery(id+"F1.opExtrude","CAP_EDGE",EDGE,{"disambiguationData":[OSD([sQuery(id+"F0.wireOp",EDGE,"E0.left")])],"isStart":true});
            var Q2;
            Q2=makeQuery(id+"F1.opExtrude","CAP_EDGE",EDGE,{"disambiguationData":[OSD([sQuery(id+"F0.wireOp",EDGE,"E0.top")])],"isStart":true});
            var Q3;
            Q3=makeQuery(id+"F1.opExtrude","CAP_EDGE",EDGE,{"disambiguationData":[OSD([sQuery(id+"F0.wireOp",EDGE,"E0.right")])],"isStart":true});
            chamfer(context, id + "F4", {"entities" : qUnion([Q0, Q1, Q2, Q3]), "width" : 1.5 * mm, "tangentPropagation" : true});
        }
    });
